# Revit family: xxxTub_Spout-GROHE-Eurosmart-13356XX3_Series
name_source: partatom
category: Plumbing Fixtures
units: mm (PartAtom-declared; Revit-internal decimal feet)

## family parameters
Cut with Voids When Loaded = No
Host = Face
OmniClass Number = 23.45.05.14.21.11
OmniClass Title = Bath/Shower Units
Part Type = Normal
Room Calculation Point = No
Round Connector Dimension = Use Diameter
Shared = Yes

## types (2) — shared parameters
ADA Compliant = Yes
Assembly Code = D2010510
CW Connection = No
CWFU = 3
Default Elevation = 24"
Description = Diverter Tub Spout
Diameter = 2 11/16"
HW Connection = No
HWFU = 3
IAPMO Compliance = ADA • CEC Certified • Massachusetts Plumbing Board Approved  • CSA B125.1 • ASME A112.18.1
Installation Type = Wall Mounted
Length = 8"
Manufacturer = Grohe
Price = Prices may vary. Please consult Manufacturer Representative for most up-to-date price list.
Product Documentation Link = https://americanstandard.box.com
Product Page URL = https://www.grohe.us
Revised Date = 10/07/2022
Spout Reach = 6 1/8"
Tempered Connection = Yes
Tempered Water Connection Diameter = 1/2"
URL = https://www.grohe.us
Vent Connection = No
WFU = 4
Waste Connection = No

## per-type parameters (varying)
| type | Finish | Material |
| 13356003 | Metal-Grohe-000-StarLight Chrome | Metal-Grohe-000-StarLight Chrome |
| 13356EN3 | Metal-Grohe-EN3-Brushed Nickel Infinity Finish | Metal-Grohe-EN3-Brushed Nickel Infinity Finish |

note: column(s) folded — value = type name in every type: Model

## geometry (parser evidence)
native form markers: Sweep x3
no freeform markers — native parametric forms only
